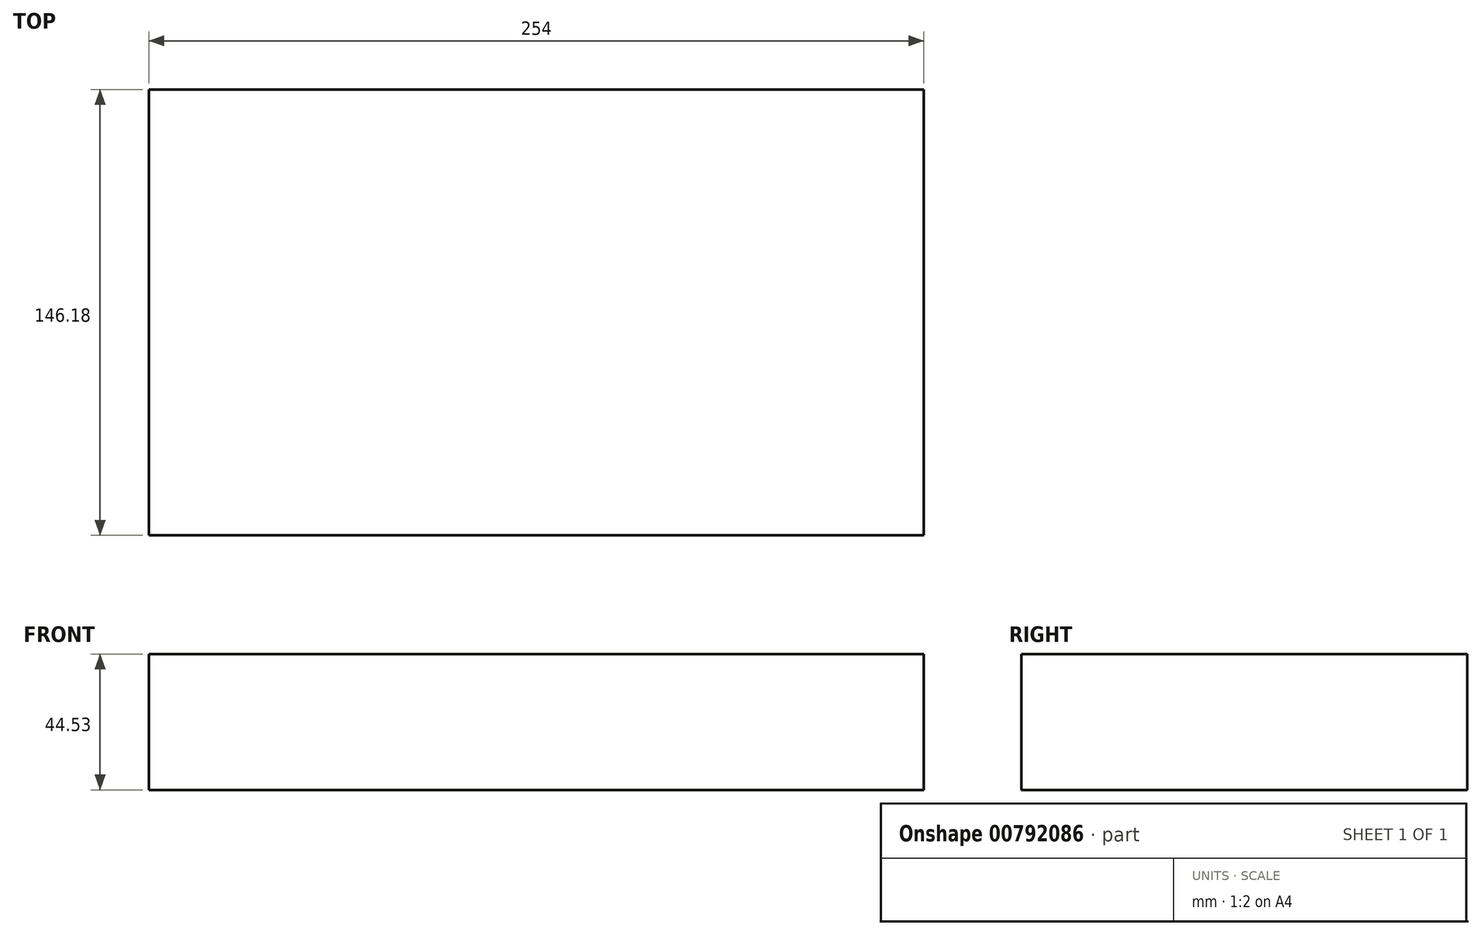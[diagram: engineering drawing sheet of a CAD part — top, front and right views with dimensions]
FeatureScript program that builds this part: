
annotation { "Feature Type Name" : "Feature", "Feature Type Description" : "" }
export const myFeature = defineFeature(function(context is Context, id is Id, definition is map)
    precondition{}
    {
        {
            var Q0;
            Q0=qCreatedBy(makeId("Right.planeOp"),FACE);
            var sketch = newSketch(context, id + "F0", { "sketchPlane" : qUnion([Q0])});
            skLineSegment(sketch, "E0.bottom", {"start": v(46.42, 8.7) * mm, "end": v(-99.76, 8.7) * mm});
            skLineSegment(sketch, "E0.top", {"start": v(46.42, 53.22) * mm, "end": v(-99.76, 53.22) * mm});
            skLineSegment(sketch, "E0.left", {"start": v(46.42, 8.7) * mm, "end": v(46.42, 53.22) * mm});
            skLineSegment(sketch, "E0.right", {"start": v(-99.76, 8.7) * mm, "end": v(-99.76, 53.22) * mm});
            skPoint(sketch, "E0.middle", {"position": v(-26.67, 30.95) * mm});
            skSolve(sketch);
        }
        {
            var Q0;
            Q0 = qSketchRegion(id + "F0", true);
            extrude(context, id + "F1", {"entities" : qUnion([Q0]), "depth" : 254 * mm, "offsetDistance" : 25.4 * mm});
        }
    });
